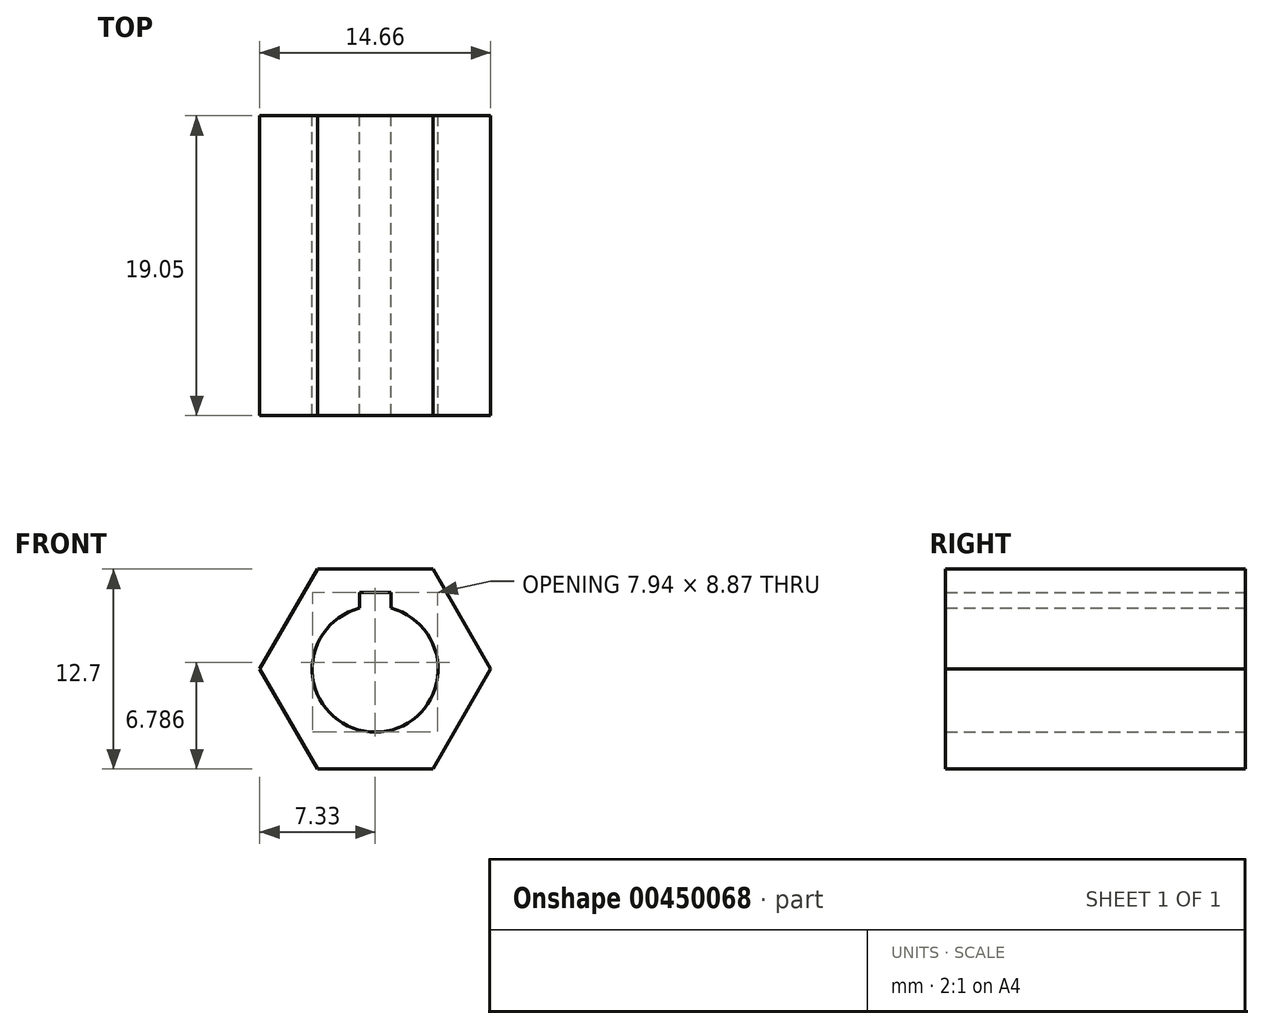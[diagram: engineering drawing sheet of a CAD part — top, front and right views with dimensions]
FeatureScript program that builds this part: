
annotation { "Feature Type Name" : "Feature", "Feature Type Description" : "" }
export const myFeature = defineFeature(function(context is Context, id is Id, definition is map)
    precondition{}
    {
        {
            var Q0;
            Q0=qCreatedBy(makeId("Front.planeOp"),FACE);
            var sketch = newSketch(context, id + "F0", { "sketchPlane" : qUnion([Q0])});
            skLineSegment(sketch, "E0", {"start": v(-3.67, 6.35) * mm, "end": v(3.67, 6.35) * mm});
            skLineSegment(sketch, "E1", {"start": v(3.67, 6.35) * mm, "end": v(7.33, 0) * mm});
            skLineSegment(sketch, "E2", {"start": v(7.33, 0) * mm, "end": v(3.67, -6.35) * mm});
            skLineSegment(sketch, "E3", {"start": v(3.67, -6.35) * mm, "end": v(-3.67, -6.35) * mm});
            skLineSegment(sketch, "E4", {"start": v(-3.67, -6.35) * mm, "end": v(-7.33, 0) * mm});
            skLineSegment(sketch, "E5", {"start": v(-7.33, 0) * mm, "end": v(-3.67, 6.35) * mm});
            skPoint(sketch, "E6", {"position": v(0, 6.35) * mm});
            skArc(sketch, "E7", {"start": v(-1, 3.87) * mm, "mid": v(0, -4) * mm, "end": v(1, 3.87) * mm});
            skLineSegment(sketch, "E8", {"start": v(-1, 3.87) * mm, "end": v(-1, 4.87) * mm});
            skLineSegment(sketch, "E9", {"start": v(-1, 4.87) * mm, "end": v(1, 4.87) * mm});
            skLineSegment(sketch, "E10", {"start": v(1, 4.87) * mm, "end": v(1, 3.87) * mm});
            skPoint(sketch, "E11", {"position": v(0, 4.87) * mm});
            skSolve(sketch);
        }
        {
            var Q0;
            Q0=makeQuery(id+"F0.imprint","IMPRINT",FACE,{"disambiguationData":[TD([[makeQuery(id+"F0.imprint","IMPRINT",EDGE,{"derivedFrom":sQuery(id+"F0.wireOp",EDGE,"E0")}),-1.0]])]});
            extrude(context, id + "F1", {"entities" : qUnion([Q0]), "depth" : 19.05 * mm});
        }
    });
